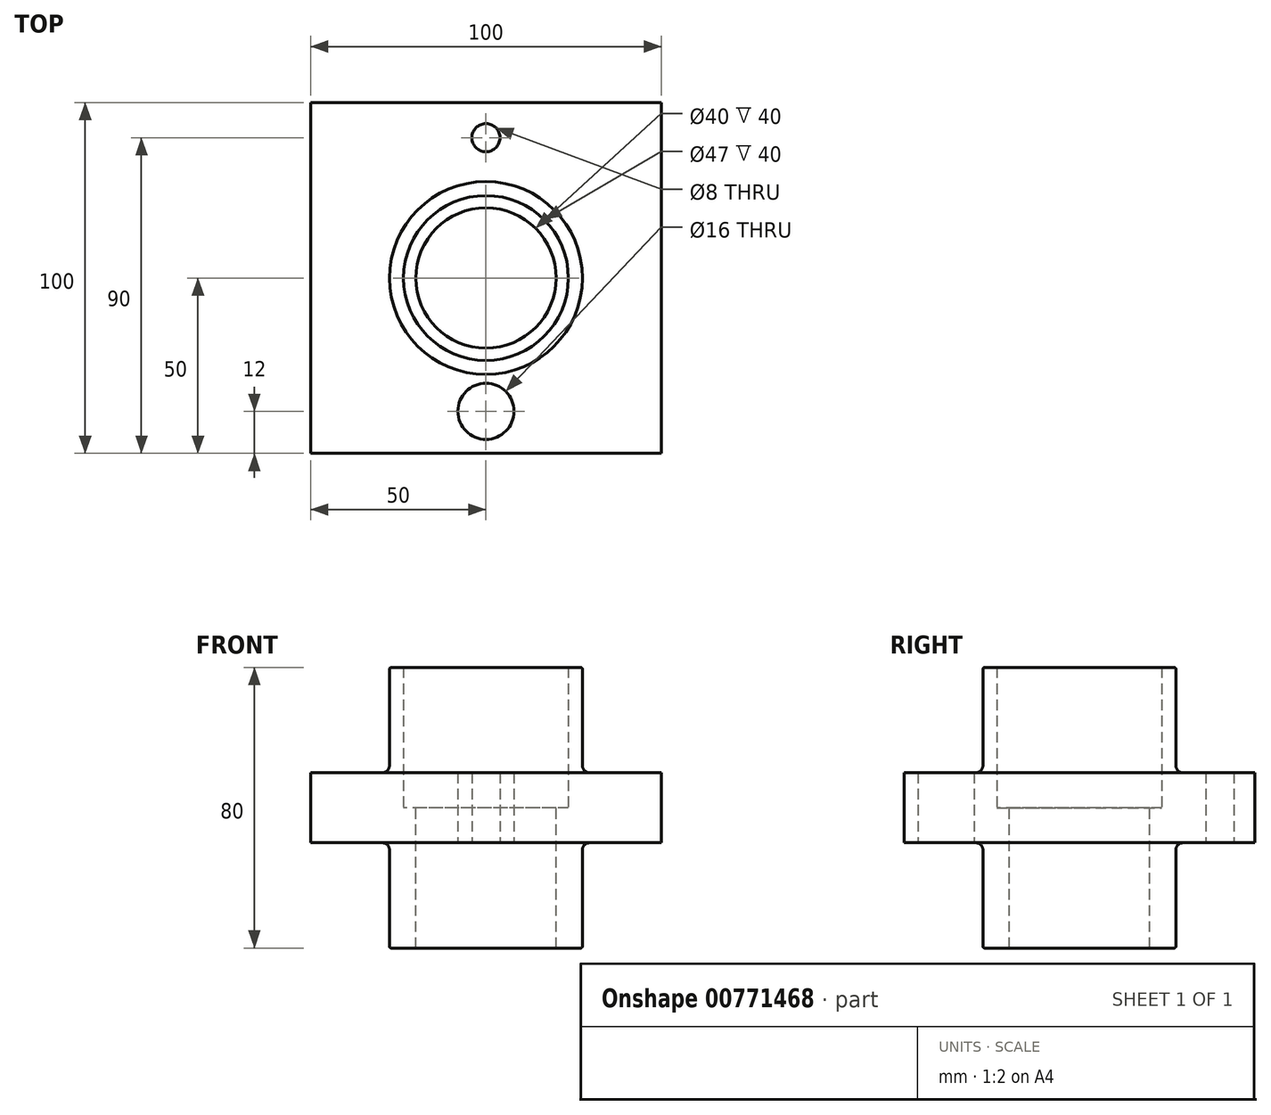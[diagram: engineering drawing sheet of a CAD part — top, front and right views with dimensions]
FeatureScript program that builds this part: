
annotation { "Feature Type Name" : "Feature", "Feature Type Description" : "" }
export const myFeature = defineFeature(function(context is Context, id is Id, definition is map)
    precondition{}
    {
        {
            var Q0;
            Q0=qCreatedBy(makeId("Top.planeOp"),FACE);
            var sketch = newSketch(context, id + "F0", { "sketchPlane" : qUnion([Q0])});
            skCircle(sketch, "E0", {"center": v(0, 0) * mm, "radius": 27.5 * mm});
            skSolve(sketch);
        }
        {
            var Q0;
            Q0=qCreatedBy(makeId("Top.planeOp"),FACE);
            var sketch = newSketch(context, id + "F1", { "sketchPlane" : qUnion([Q0])});
            skCircle(sketch, "E1", {"center": v(0, 0) * mm, "radius": 23.5 * mm});
            skSolve(sketch);
        }
        {
            var Q0;
            Q0 = qSketchRegion(id + "F0", true);
            extrude(context, id + "F2", {"entities" : qUnion([Q0]), "endBound" : BoundingType.SYMMETRIC, "depth" : 80 * mm, "offsetDistance" : 25 * mm});
        }
        {
            var Q0;
            Q0=qCreatedBy(makeId("Top.planeOp"),FACE);
            var sketch = newSketch(context, id + "F3", { "sketchPlane" : qUnion([Q0])});
            skCircle(sketch, "E2", {"center": v(0, 0) * mm, "radius": 20 * mm});
            skSolve(sketch);
        }
        {
            var Q0;
            Q0=qCreatedBy(makeId("Top.planeOp"),FACE);
            var sketch = newSketch(context, id + "F4", { "sketchPlane" : qUnion([Q0])});
            skLineSegment(sketch, "E3.bottom", {"start": v(50, -50) * mm, "end": v(-50, -50) * mm});
            skLineSegment(sketch, "E3.top", {"start": v(50, 50) * mm, "end": v(-50, 50) * mm});
            skLineSegment(sketch, "E3.left", {"start": v(50, -50) * mm, "end": v(50, 50) * mm});
            skLineSegment(sketch, "E3.right", {"start": v(-50, -50) * mm, "end": v(-50, 50) * mm});
            skPoint(sketch, "E3.middle", {"position": v(0, 0) * mm});
            skSolve(sketch);
        }
        {
            var Q0;
            Q0 = qSketchRegion(id + "F4", true);
            extrude(context, id + "F5", {"entities" : qUnion([Q0]), "operationType" : NewBodyOperationType.ADD, "endBound" : BoundingType.SYMMETRIC, "oppositeDirection" : true, "depth" : 20 * mm, "offsetDistance" : 25 * mm});
        }
        {
            var Q0;
            Q0 = qSketchRegion(id + "F3", true);
            extrude(context, id + "F6", {"entities" : qUnion([Q0]), "operationType" : NewBodyOperationType.REMOVE, "endBound" : BoundingType.THROUGH_ALL, "oppositeDirection" : true, "depth" : 25 * mm, "offsetDistance" : 25 * mm});
        }
        {
            var Q0;
            Q0 = qSketchRegion(id + "F1", true);
            extrude(context, id + "F7", {"entities" : qUnion([Q0]), "operationType" : NewBodyOperationType.REMOVE, "endBound" : BoundingType.THROUGH_ALL, "depth" : 25 * mm, "offsetDistance" : 25 * mm});
        }
        {
            var Q0;
            Q0=qCreatedBy(makeId("Top.planeOp"),FACE);
            var sketch = newSketch(context, id + "F8", { "sketchPlane" : qUnion([Q0])});
            skCircle(sketch, "E4", {"center": v(0, -38) * mm, "radius": 8 * mm});
            skSolve(sketch);
        }
        {
            var Q0;
            Q0=qCreatedBy(makeId("Top.planeOp"),FACE);
            var sketch = newSketch(context, id + "F9", { "sketchPlane" : qUnion([Q0])});
            skCircle(sketch, "E5", {"center": v(0, 40) * mm, "radius": 4 * mm});
            skSolve(sketch);
        }
        {
            var Q0;
            Q0=makeQuery(id+"F5.boolean.opBoolean","INTERSECT",EDGE,{"derivedFrom":[makeQuery(id+"F2.opExtrude","SWEPT_FACE",FACE,{"disambiguationData":[OSD([sQuery(id+"F0.wireOp",EDGE,"E0")])]}),makeQuery(id+"F5.opExtrude","CAP_FACE",FACE,{"disambiguationData":[OSD([sQuery(id+"F4.wireOp",EDGE,"E3.bottom"),sQuery(id+"F4.wireOp",EDGE,"E3.top"),sQuery(id+"F4.wireOp",EDGE,"E3.left"),sQuery(id+"F4.wireOp",EDGE,"E3.right")])],"isStart":true})]});
            var Q1;
            Q1=makeQuery(id+"F5.boolean.opBoolean","INTERSECT",EDGE,{"derivedFrom":[makeQuery(id+"F2.opExtrude","SWEPT_FACE",FACE,{"disambiguationData":[OSD([sQuery(id+"F0.wireOp",EDGE,"E0")])]}),makeQuery(id+"F5.opExtrude","CAP_FACE",FACE,{"disambiguationData":[OSD([sQuery(id+"F4.wireOp",EDGE,"E3.bottom"),sQuery(id+"F4.wireOp",EDGE,"E3.top"),sQuery(id+"F4.wireOp",EDGE,"E3.left"),sQuery(id+"F4.wireOp",EDGE,"E3.right")])],"isStart":false})]});
            fillet(context, id + "F10", {"entities" : qUnion([Q0, Q1]), "radius" : 2 * mm, "tangentPropagation" : true, "allowEdgeOverflow" : false});
        }
        {
            var Q0;
            Q0=makeQuery(id+"F2.opExtrude","CAP_EDGE",EDGE,{"disambiguationData":[OSD([sQuery(id+"F0.wireOp",EDGE,"E0")])],"isStart":true});
            var Q1;
            Q1=makeQuery(id+"F2.opExtrude","CAP_EDGE",EDGE,{"disambiguationData":[OSD([sQuery(id+"F0.wireOp",EDGE,"E0")])],"isStart":false});
            fillet(context, id + "F11", {"entities" : qUnion([Q0, Q1]), "radius" : 0.5 * mm, "tangentPropagation" : true, "allowEdgeOverflow" : false});
        }
        {
            var Q0;
            Q0 = qSketchRegion(id + "F8", true);
            var Q1;
            Q1 = qSketchRegion(id + "F9", true);
            extrude(context, id + "F12", {"entities" : qUnion([Q0, Q1]), "operationType" : NewBodyOperationType.REMOVE, "endBound" : BoundingType.SYMMETRIC, "depth" : 30 * mm, "offsetDistance" : 25 * mm});
        }
    });
